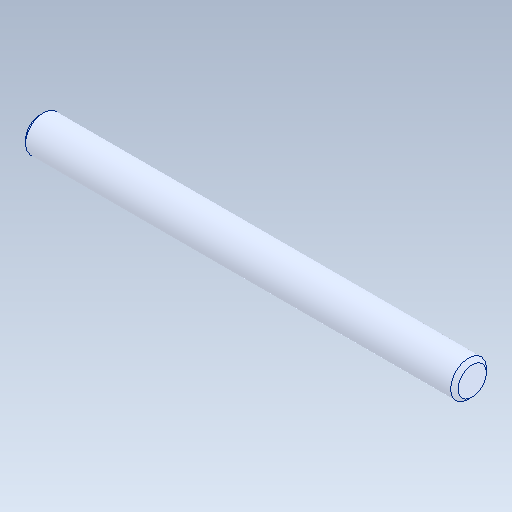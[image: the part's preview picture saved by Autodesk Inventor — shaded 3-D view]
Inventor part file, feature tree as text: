
AUTODESK INVENTOR PART (.ipt)
format: ipt  version: 2020 (Build 240168000, 168)  size: 86,528 bytes
history: native  units: in
note: dims shown in document units (in); Inventor stores cm internally (conversion verified against a paired STEP export)
features: chamfer x1
ambient origin geometry x8: Origin, YZ Plane, XZ Plane, XY Plane, X Axis, Y Axis, Z Axis, Center Point
bodies: Solid1 (feature_tree)
feature tree (1):
  chamfer  "Chamfer1"  [1 undecoded]
note: 1 required parameter value undecoded (feature->parameter linkage not recoverable at this tier; creation-order binding heuristic only, values carry confidence <= 0.55)
